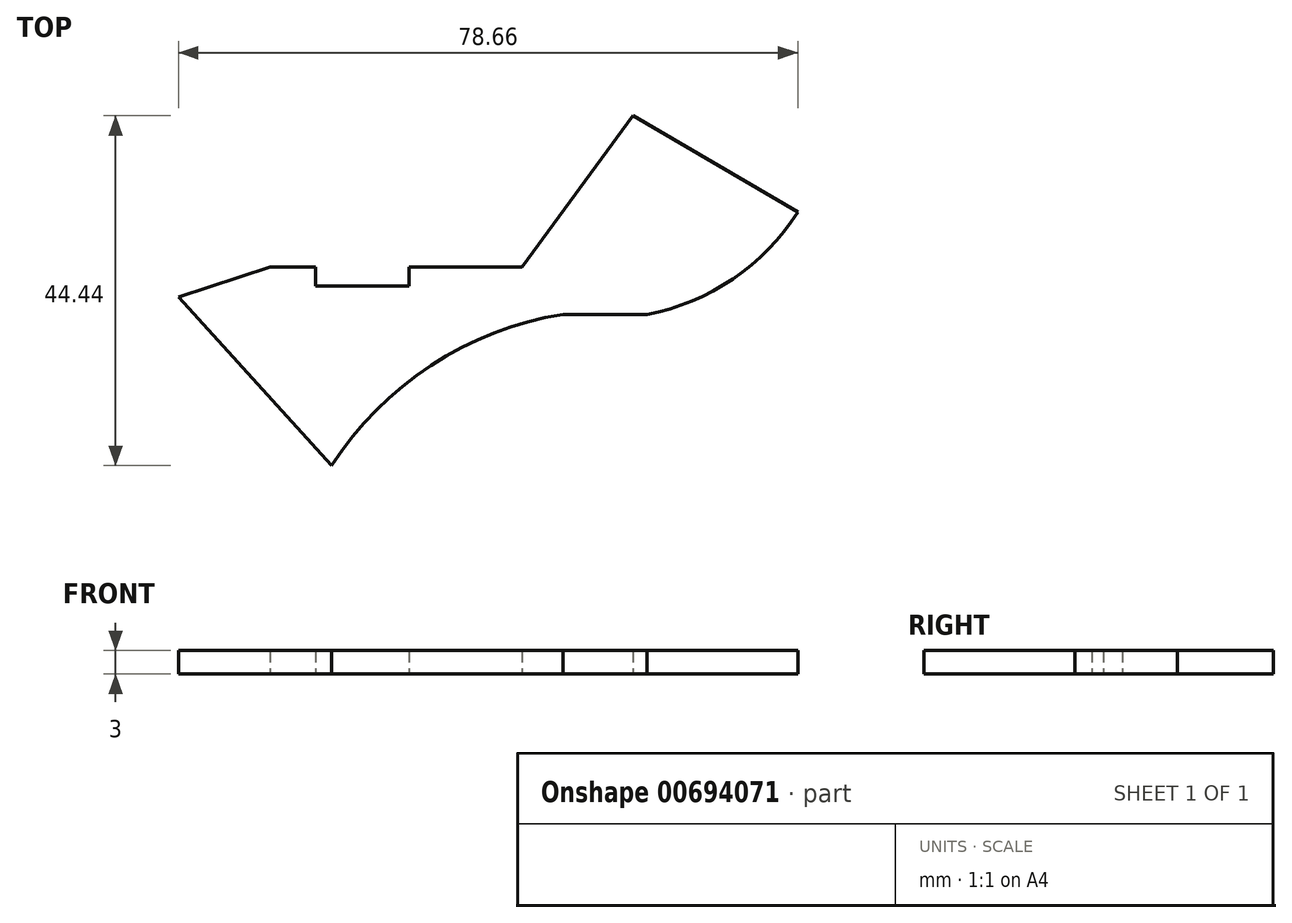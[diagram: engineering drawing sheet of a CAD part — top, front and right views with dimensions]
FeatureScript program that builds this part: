
annotation { "Feature Type Name" : "Feature", "Feature Type Description" : "" }
export const myFeature = defineFeature(function(context is Context, id is Id, definition is map)
    precondition{}
    {
        {
            var Q0;
            Q0=qCreatedBy(makeId("Top.planeOp"),FACE);
            var sketch = newSketch(context, id + "F0", { "sketchPlane" : qUnion([Q0])});
            skLineSegment(sketch, "E0", {"start": v(0, 0) * mm, "end": v(0, 2.42) * mm});
            skLineSegment(sketch, "E1", {"start": v(0, 2.42) * mm, "end": v(-5.8, 2.42) * mm});
            skLineSegment(sketch, "E2", {"start": v(0, 0) * mm, "end": v(11.85, 0) * mm});
            skLineSegment(sketch, "E3", {"start": v(11.85, 0) * mm, "end": v(11.85, 2.42) * mm});
            skLineSegment(sketch, "E4", {"start": v(-5.8, 2.42) * mm, "end": v(-17.43, 2.42) * mm});
            skLineSegment(sketch, "E5", {"start": v(-17.43, 2.42) * mm, "end": v(-17.43, -1.42) * mm});
            skLineSegment(sketch, "E6", {"start": v(-17.43, -1.42) * mm, "end": v(-5.8, 2.42) * mm});
            skLineSegment(sketch, "E7", {"start": v(-17.43, -1.42) * mm, "end": v(-17.43, -22.8) * mm});
            skLineSegment(sketch, "E8", {"start": v(-17.43, -22.8) * mm, "end": v(2.02, -22.8) * mm});
            skLineSegment(sketch, "E9", {"start": v(2.02, -22.81) * mm, "end": v(-17.43, -1.42) * mm});
            skLineSegment(sketch, "E10", {"start": v(2.02, -22.8) * mm, "end": v(31.38, -22.8) * mm});
            skLineSegment(sketch, "E11", {"start": v(31.38, -22.8) * mm, "end": v(31.38, -3.6) * mm});
            skLineSegment(sketch, "E12", {"start": v(31.38, -3.6) * mm, "end": v(2.02, -22.8) * mm});
            skLineSegment(sketch, "E13", {"start": v(16.7, -13.2) * mm, "end": v(14.66, -10.1) * mm});
            skLineSegment(sketch, "E14", {"start": v(31.38, -3.6) * mm, "end": v(61.23, -3.6) * mm});
            skLineSegment(sketch, "E15", {"start": v(61.23, -3.6) * mm, "end": v(61.23, 9.4) * mm});
            skLineSegment(sketch, "E16", {"start": v(61.23, 9.4) * mm, "end": v(31.38, -3.6) * mm});
            skLineSegment(sketch, "E17", {"start": v(46.3, 2.9) * mm, "end": v(48.3, -1.69) * mm});
            skLineSegment(sketch, "E18", {"start": v(61.23, 9.4) * mm, "end": v(61.23, 21.63) * mm});
            skLineSegment(sketch, "E19", {"start": v(61.23, 21.63) * mm, "end": v(40.32, 21.63) * mm});
            skLineSegment(sketch, "E20", {"start": v(40.32, 21.63) * mm, "end": v(61.23, 9.4) * mm});
            skLineSegment(sketch, "E21", {"start": v(40.32, 21.63) * mm, "end": v(25.1, 21.63) * mm});
            skLineSegment(sketch, "E22", {"start": v(25.1, 21.63) * mm, "end": v(25.1, 0.91) * mm});
            skLineSegment(sketch, "E23", {"start": v(25.1, 0.91) * mm, "end": v(40.32, 21.63) * mm});
            skLineSegment(sketch, "E24", {"start": v(11.85, 2.42) * mm, "end": v(25.1, 2.42) * mm});
            skLineSegment(sketch, "E25", {"start": v(25.1, 2.42) * mm, "end": v(26.2, 2.42) * mm});
            skArc(sketch, "E26", {"start": v(31.38, -3.61) * mm, "mid": v(14.66, -10.1) * mm, "end": v(2.02, -22.81) * mm});
            skArc(sketch, "E27", {"start": v(31.38, -3.6) * mm, "mid": v(48.3, -1.69) * mm, "end": v(61.23, 9.4) * mm});
            skSolve(sketch);
        }
        {
            var Q0;
            Q0=makeQuery(id+"F0.imprint","IMPRINT",FACE,{"disambiguationData":[TD([[makeQuery(id+"F0.imprint","IMPRINT",EDGE,{"derivedFrom":sQuery(id+"F0.wireOp",EDGE,"E0")}),1.0]])]});
            var Q1;
            {var subQ3=sQuery(id+"F0.wireOp",EDGE,"E17");Q1=makeQuery(id+"F0.imprint","IMPRINT",FACE,{"disambiguationData":[TD([[makeQuery(id+"F0.imprint","IMPRINT",EDGE,{"derivedFrom":subQ3}),1.0]])]});}
            var Q2;
            {var subQ5=sQuery(id+"F0.wireOp",EDGE,"E17");Q2=makeQuery(id+"F0.imprint","IMPRINT",FACE,{"disambiguationData":[TD([[makeQuery(id+"F0.imprint","IMPRINT",EDGE,{"derivedFrom":subQ5}),-1.0]])]});}
            var Q3;
            {var subQ3=sQuery(id+"F0.wireOp",EDGE,"E25");Q3=makeQuery(id+"F0.imprint","IMPRINT",FACE,{"disambiguationData":[TD([[makeQuery(id+"F0.imprint","IMPRINT",EDGE,{"derivedFrom":subQ3}),-1.0]])]});}
            extrude(context, id + "F1", {"entities" : qUnion([Q0, Q1, Q2, Q3]), "depth" : 3 * mm, "offsetDistance" : 25.4 * mm});
        }
    });
